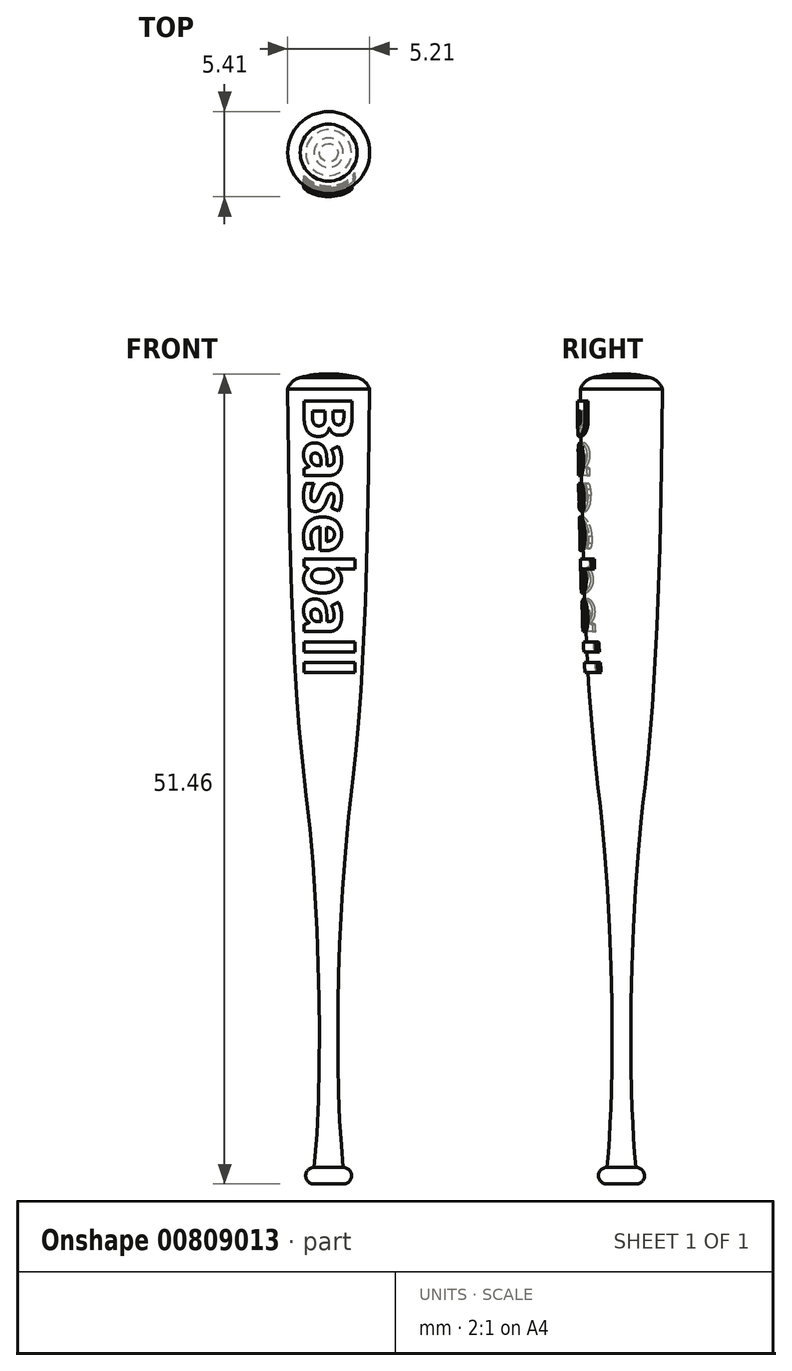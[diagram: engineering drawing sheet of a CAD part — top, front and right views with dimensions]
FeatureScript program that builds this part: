
annotation { "Feature Type Name" : "Feature", "Feature Type Description" : "" }
export const myFeature = defineFeature(function(context is Context, id is Id, definition is map)
    precondition{}
    {
        {
            var Q0;
            Q0=qCreatedBy(makeId("Front.planeOp"),FACE);
            var sketch = newSketch(context, id + "F0", { "sketchPlane" : qUnion([Q0])});
            skFitSpline(sketch, "E0", {"points": [v(-3.44, 24.76) * mm, v(-4.8, -2.6) * mm, v(-5.43, -13.25) * mm, v(-5.12, -24.67) * mm], "startDerivative": vector(-1.3, -133.52) * mm, "endDerivative": vector(3.27, -30.05) * mm});
            skArc(sketch, "E1", {"start": v(-3.44, 24.76) * mm, "mid": v(-3.74, 25.24) * mm, "end": v(-4.24, 25.5) * mm});
            skArc(sketch, "E2", {"start": v(-5.12, -25.72) * mm, "mid": v(-4.59, -25.2) * mm, "end": v(-5.12, -24.67) * mm});
            skArc(sketch, "E3", {"start": v(-4.24, 25.5) * mm, "mid": v(-5.14, 25.68) * mm, "end": v(-6.05, 25.74) * mm});
            skLineSegment(sketch, "E4", {"start": v(-6.05, -25.72) * mm, "end": v(-5.12, -25.72) * mm});
            skFitSpline(sketch, "E5", {"points": [v(6.48, 24.76) * mm, v(5.45, -2.22) * mm, v(4.49, -13.25) * mm, v(4.8, -24.67) * mm], "startDerivative": vector(-1.07, -189.4) * mm, "endDerivative": vector(3.27, -30.05) * mm});
            skArc(sketch, "E6", {"start": v(6.48, 24.76) * mm, "mid": v(6.18, 25.24) * mm, "end": v(5.68, 25.5) * mm});
            skArc(sketch, "E7", {"start": v(4.8, -25.72) * mm, "mid": v(5.33, -25.2) * mm, "end": v(4.8, -24.67) * mm});
            skArc(sketch, "E8", {"start": v(5.68, 25.5) * mm, "mid": v(4.79, 25.68) * mm, "end": v(3.87, 25.74) * mm});
            skLineSegment(sketch, "E9", {"start": v(3.87, -25.72) * mm, "end": v(4.8, -25.72) * mm});
            skLineSegment(sketch, "E10", {"start": v(3.87, 25.74) * mm, "end": v(3.87, 24.94) * mm});
            skLineSegment(sketch, "E11", {"start": v(-6.05, 25.74) * mm, "end": v(-6.05, -25.72) * mm});
            skLineSegment(sketch, "E12", {"start": v(3.87, 24.94) * mm, "end": v(3.87, -25.72) * mm});
            skSolve(sketch);
        }
        {
            var Q0;
            Q0=qCreatedBy(makeId("Front.planeOp"),FACE);
            var sketch = newSketch(context, id + "F1", { "sketchPlane" : qUnion([Q0])});
            skText(sketch, "E13", { "text": "Softball", "fontName": "OpenSans-Bold.ttf"});
            skText(sketch, "E14", { "text": "Baseball", "fontName": "OpenSans-Bold.ttf"});
            const initialGuessF1  = {"E13": [0.00236, 0.02362, 0, -1, 0.00307], "E14": [-0.0076, 0.0244, 0, -1, 0.00307]};
            skSetInitialGuess(sketch, initialGuessF1);
            skSolve(sketch);
        }
        {
            var Q0;
            Q0=makeQuery(id+"F0.imprint","IMPRINT",FACE,{"disambiguationData":[TD([[makeQuery(id+"F0.imprint","IMPRINT",EDGE,{"derivedFrom":sQuery(id+"F0.wireOp",EDGE,"E5")}),-1.0]])]});
            var Q1;
            Q1=sQuery(id+"F0.wireOp",EDGE,"E12");
            revolve(context, id + "F2", {"surfaceOperationType" : NewSurfaceOperationType.NEW, "entities" : qUnion([Q0]), "axis" : qUnion([Q1]), "revolveType" : RevolveType.FULL});
        }
        {
            var Q0;
            Q0 = qSketchRegion(id + "F1", true);
            var Q1;
            Q1=makeQuery(id+"F2.opRevolve","SWEPT_BODY",BODY,{"disambiguationData":[OSD([sQuery(id+"F0.wireOp",EDGE,"E5"),sQuery(id+"F0.wireOp",EDGE,"E6"),sQuery(id+"F0.wireOp",EDGE,"E7"),sQuery(id+"F0.wireOp",EDGE,"E8"),sQuery(id+"F0.wireOp",EDGE,"E9"),sQuery(id+"F0.wireOp",EDGE,"E10"),sQuery(id+"F0.wireOp",EDGE,"E12")])]});
            extrude(context, id + "F3", {"entities" : qUnion([Q0]), "operationType" : NewBodyOperationType.INTERSECT, "depth" : 2.8 * mm, "endBoundEntityBody" : qUnion([Q1]), "offsetDistance" : 25 * mm});
        }
        {
            var Q0;
            Q0=makeQuery(id+"F3.boolean.opBoolean","SPLIT",BODY,{"disambiguationData":[OD(0.0)],"derivedFrom":makeQuery(id+"F2.opRevolve","SWEPT_BODY",BODY,{"disambiguationData":[OSD([sQuery(id+"F0.wireOp",EDGE,"E5"),sQuery(id+"F0.wireOp",EDGE,"E6"),sQuery(id+"F0.wireOp",EDGE,"E7"),sQuery(id+"F0.wireOp",EDGE,"E8"),sQuery(id+"F0.wireOp",EDGE,"E9"),sQuery(id+"F0.wireOp",EDGE,"E10"),sQuery(id+"F0.wireOp",EDGE,"E12")])]})});
            var Q1;
            Q1=makeQuery(id+"F3.boolean.opBoolean","SPLIT",BODY,{"disambiguationData":[OD(1.0)],"derivedFrom":makeQuery(id+"F2.opRevolve","SWEPT_BODY",BODY,{"disambiguationData":[OSD([sQuery(id+"F0.wireOp",EDGE,"E5"),sQuery(id+"F0.wireOp",EDGE,"E6"),sQuery(id+"F0.wireOp",EDGE,"E7"),sQuery(id+"F0.wireOp",EDGE,"E8"),sQuery(id+"F0.wireOp",EDGE,"E9"),sQuery(id+"F0.wireOp",EDGE,"E10"),sQuery(id+"F0.wireOp",EDGE,"E12")])]})});
            var Q2;
            Q2=makeQuery(id+"F3.boolean.opBoolean","SPLIT",BODY,{"disambiguationData":[OD(2.0)],"derivedFrom":makeQuery(id+"F2.opRevolve","SWEPT_BODY",BODY,{"disambiguationData":[OSD([sQuery(id+"F0.wireOp",EDGE,"E5"),sQuery(id+"F0.wireOp",EDGE,"E6"),sQuery(id+"F0.wireOp",EDGE,"E7"),sQuery(id+"F0.wireOp",EDGE,"E8"),sQuery(id+"F0.wireOp",EDGE,"E9"),sQuery(id+"F0.wireOp",EDGE,"E10"),sQuery(id+"F0.wireOp",EDGE,"E12")])]})});
            var Q3;
            Q3=makeQuery(id+"F3.boolean.opBoolean","SPLIT",BODY,{"disambiguationData":[OD(3.0)],"derivedFrom":makeQuery(id+"F2.opRevolve","SWEPT_BODY",BODY,{"disambiguationData":[OSD([sQuery(id+"F0.wireOp",EDGE,"E5"),sQuery(id+"F0.wireOp",EDGE,"E6"),sQuery(id+"F0.wireOp",EDGE,"E7"),sQuery(id+"F0.wireOp",EDGE,"E8"),sQuery(id+"F0.wireOp",EDGE,"E9"),sQuery(id+"F0.wireOp",EDGE,"E10"),sQuery(id+"F0.wireOp",EDGE,"E12")])]})});
            var Q4;
            Q4=makeQuery(id+"F3.boolean.opBoolean","SPLIT",BODY,{"disambiguationData":[OD(4.0)],"derivedFrom":makeQuery(id+"F2.opRevolve","SWEPT_BODY",BODY,{"disambiguationData":[OSD([sQuery(id+"F0.wireOp",EDGE,"E5"),sQuery(id+"F0.wireOp",EDGE,"E6"),sQuery(id+"F0.wireOp",EDGE,"E7"),sQuery(id+"F0.wireOp",EDGE,"E8"),sQuery(id+"F0.wireOp",EDGE,"E9"),sQuery(id+"F0.wireOp",EDGE,"E10"),sQuery(id+"F0.wireOp",EDGE,"E12")])]})});
            var Q5;
            Q5=makeQuery(id+"F3.boolean.opBoolean","SPLIT",BODY,{"disambiguationData":[OD(5.0)],"derivedFrom":makeQuery(id+"F2.opRevolve","SWEPT_BODY",BODY,{"disambiguationData":[OSD([sQuery(id+"F0.wireOp",EDGE,"E5"),sQuery(id+"F0.wireOp",EDGE,"E6"),sQuery(id+"F0.wireOp",EDGE,"E7"),sQuery(id+"F0.wireOp",EDGE,"E8"),sQuery(id+"F0.wireOp",EDGE,"E9"),sQuery(id+"F0.wireOp",EDGE,"E10"),sQuery(id+"F0.wireOp",EDGE,"E12")])]})});
            var Q6;
            Q6=makeQuery(id+"F3.boolean.opBoolean","SPLIT",BODY,{"disambiguationData":[OD(6.0)],"derivedFrom":makeQuery(id+"F2.opRevolve","SWEPT_BODY",BODY,{"disambiguationData":[OSD([sQuery(id+"F0.wireOp",EDGE,"E5"),sQuery(id+"F0.wireOp",EDGE,"E6"),sQuery(id+"F0.wireOp",EDGE,"E7"),sQuery(id+"F0.wireOp",EDGE,"E8"),sQuery(id+"F0.wireOp",EDGE,"E9"),sQuery(id+"F0.wireOp",EDGE,"E10"),sQuery(id+"F0.wireOp",EDGE,"E12")])]})});
            var Q7;
            Q7=makeQuery(id+"F3.boolean.opBoolean","SPLIT",BODY,{"disambiguationData":[OD(7.0)],"derivedFrom":makeQuery(id+"F2.opRevolve","SWEPT_BODY",BODY,{"disambiguationData":[OSD([sQuery(id+"F0.wireOp",EDGE,"E5"),sQuery(id+"F0.wireOp",EDGE,"E6"),sQuery(id+"F0.wireOp",EDGE,"E7"),sQuery(id+"F0.wireOp",EDGE,"E8"),sQuery(id+"F0.wireOp",EDGE,"E9"),sQuery(id+"F0.wireOp",EDGE,"E10"),sQuery(id+"F0.wireOp",EDGE,"E12")])]})});
            transform(context, id + "F4", {"entities" : qUnion([Q0, Q1, Q2, Q3, Q4, Q5, Q6, Q7]), "transformType" : TransformType.TRANSLATION_3D, "dx" : 0 * mm, "dy" : -0.2 * mm, "dz" : 0 * mm, "makeCopy" : false});
        }
        {
            var Q0;
            Q0=makeQuery(id+"F0.imprint","IMPRINT",FACE,{"disambiguationData":[TD([[makeQuery(id+"F0.imprint","IMPRINT",EDGE,{"derivedFrom":sQuery(id+"F0.wireOp",EDGE,"E5")}),-1.0]])]});
            var Q1;
            Q1=sQuery(id+"F0.wireOp",EDGE,"E12");
            revolve(context, id + "F5", {"operationType" : NewBodyOperationType.ADD, "surfaceOperationType" : NewSurfaceOperationType.NEW, "entities" : qUnion([Q0]), "axis" : qUnion([Q1]), "revolveType" : RevolveType.FULL});
        }
        {
            var Q0;
            Q0=makeQuery(id+"F0.imprint","IMPRINT",FACE,{"disambiguationData":[TD([[makeQuery(id+"F0.imprint","IMPRINT",EDGE,{"derivedFrom":sQuery(id+"F0.wireOp",EDGE,"E0")}),-1.0]])]});
            var Q1;
            Q1=sQuery(id+"F0.wireOp",EDGE,"E11");
            revolve(context, id + "F6", {"surfaceOperationType" : NewSurfaceOperationType.NEW, "entities" : qUnion([Q0]), "axis" : qUnion([Q1]), "revolveType" : RevolveType.FULL});
        }
        {
            var Q0;
            Q0=makeQuery(id+"F1.imprint","IMPRINT",FACE,{"disambiguationData":[TD([[makeQuery(id+"F1.imprint","IMPRINT",EDGE,{"derivedFrom":sQuery(id+"F1.wireOp",EDGE,"E14.sketch_text.stroke-0")}),-1.0]])]});
            var Q1;
            Q1=makeQuery(id+"F1.imprint","IMPRINT",FACE,{"disambiguationData":[TD([[makeQuery(id+"F1.imprint","IMPRINT",EDGE,{"derivedFrom":sQuery(id+"F1.wireOp",EDGE,"E14.sketch_text.stroke-25")}),-1.0]])]});
            var Q2;
            Q2=makeQuery(id+"F1.imprint","IMPRINT",FACE,{"disambiguationData":[TD([[makeQuery(id+"F1.imprint","IMPRINT",EDGE,{"derivedFrom":sQuery(id+"F1.wireOp",EDGE,"E14.sketch_text.stroke-52")}),-1.0]])]});
            var Q3;
            Q3=makeQuery(id+"F1.imprint","IMPRINT",FACE,{"disambiguationData":[TD([[makeQuery(id+"F1.imprint","IMPRINT",EDGE,{"derivedFrom":sQuery(id+"F1.wireOp",EDGE,"E14.sketch_text.stroke-77")}),-1.0]])]});
            var Q4;
            Q4=makeQuery(id+"F1.imprint","IMPRINT",FACE,{"disambiguationData":[TD([[makeQuery(id+"F1.imprint","IMPRINT",EDGE,{"derivedFrom":sQuery(id+"F1.wireOp",EDGE,"E14.sketch_text.stroke-96")}),-1.0]])]});
            var Q5;
            Q5=makeQuery(id+"F1.imprint","IMPRINT",FACE,{"disambiguationData":[TD([[makeQuery(id+"F1.imprint","IMPRINT",EDGE,{"derivedFrom":sQuery(id+"F1.wireOp",EDGE,"E14.sketch_text.stroke-119")}),-1.0]])]});
            var Q6;
            Q6=makeQuery(id+"F1.imprint","IMPRINT",FACE,{"disambiguationData":[TD([[makeQuery(id+"F1.imprint","IMPRINT",EDGE,{"derivedFrom":sQuery(id+"F1.wireOp",EDGE,"E14.sketch_text.stroke-146")}),-1.0]])]});
            var Q7;
            Q7=makeQuery(id+"F1.imprint","IMPRINT",FACE,{"disambiguationData":[TD([[makeQuery(id+"F1.imprint","IMPRINT",EDGE,{"derivedFrom":sQuery(id+"F1.wireOp",EDGE,"E14.sketch_text.stroke-150")}),-1.0]])]});
            extrude(context, id + "F7", {"entities" : qUnion([Q0, Q1, Q2, Q3, Q4, Q5, Q6, Q7]), "operationType" : NewBodyOperationType.INTERSECT, "depth" : 25 * mm, "offsetDistance" : 25 * mm});
        }
        {
            var Q0;
            Q0=makeQuery(id+"F7.boolean.opBoolean","SPLIT",BODY,{"disambiguationData":[OD(0.0)],"derivedFrom":makeQuery(id+"F6.opRevolve","SWEPT_BODY",BODY,{"disambiguationData":[OSD([sQuery(id+"F0.wireOp",EDGE,"E0"),sQuery(id+"F0.wireOp",EDGE,"E1"),sQuery(id+"F0.wireOp",EDGE,"E2"),sQuery(id+"F0.wireOp",EDGE,"E3"),sQuery(id+"F0.wireOp",EDGE,"E4"),sQuery(id+"F0.wireOp",EDGE,"E11")])]})});
            var Q1;
            Q1=makeQuery(id+"F7.boolean.opBoolean","SPLIT",BODY,{"disambiguationData":[OD(1.0)],"derivedFrom":makeQuery(id+"F6.opRevolve","SWEPT_BODY",BODY,{"disambiguationData":[OSD([sQuery(id+"F0.wireOp",EDGE,"E0"),sQuery(id+"F0.wireOp",EDGE,"E1"),sQuery(id+"F0.wireOp",EDGE,"E2"),sQuery(id+"F0.wireOp",EDGE,"E3"),sQuery(id+"F0.wireOp",EDGE,"E4"),sQuery(id+"F0.wireOp",EDGE,"E11")])]})});
            var Q2;
            Q2=makeQuery(id+"F7.boolean.opBoolean","SPLIT",BODY,{"disambiguationData":[OD(2.0)],"derivedFrom":makeQuery(id+"F6.opRevolve","SWEPT_BODY",BODY,{"disambiguationData":[OSD([sQuery(id+"F0.wireOp",EDGE,"E0"),sQuery(id+"F0.wireOp",EDGE,"E1"),sQuery(id+"F0.wireOp",EDGE,"E2"),sQuery(id+"F0.wireOp",EDGE,"E3"),sQuery(id+"F0.wireOp",EDGE,"E4"),sQuery(id+"F0.wireOp",EDGE,"E11")])]})});
            var Q3;
            Q3=makeQuery(id+"F7.boolean.opBoolean","SPLIT",BODY,{"disambiguationData":[OD(3.0)],"derivedFrom":makeQuery(id+"F6.opRevolve","SWEPT_BODY",BODY,{"disambiguationData":[OSD([sQuery(id+"F0.wireOp",EDGE,"E0"),sQuery(id+"F0.wireOp",EDGE,"E1"),sQuery(id+"F0.wireOp",EDGE,"E2"),sQuery(id+"F0.wireOp",EDGE,"E3"),sQuery(id+"F0.wireOp",EDGE,"E4"),sQuery(id+"F0.wireOp",EDGE,"E11")])]})});
            var Q4;
            Q4=makeQuery(id+"F7.boolean.opBoolean","SPLIT",BODY,{"disambiguationData":[OD(4.0)],"derivedFrom":makeQuery(id+"F6.opRevolve","SWEPT_BODY",BODY,{"disambiguationData":[OSD([sQuery(id+"F0.wireOp",EDGE,"E0"),sQuery(id+"F0.wireOp",EDGE,"E1"),sQuery(id+"F0.wireOp",EDGE,"E2"),sQuery(id+"F0.wireOp",EDGE,"E3"),sQuery(id+"F0.wireOp",EDGE,"E4"),sQuery(id+"F0.wireOp",EDGE,"E11")])]})});
            var Q5;
            Q5=makeQuery(id+"F7.boolean.opBoolean","SPLIT",BODY,{"disambiguationData":[OD(5.0)],"derivedFrom":makeQuery(id+"F6.opRevolve","SWEPT_BODY",BODY,{"disambiguationData":[OSD([sQuery(id+"F0.wireOp",EDGE,"E0"),sQuery(id+"F0.wireOp",EDGE,"E1"),sQuery(id+"F0.wireOp",EDGE,"E2"),sQuery(id+"F0.wireOp",EDGE,"E3"),sQuery(id+"F0.wireOp",EDGE,"E4"),sQuery(id+"F0.wireOp",EDGE,"E11")])]})});
            var Q6;
            Q6=makeQuery(id+"F7.boolean.opBoolean","SPLIT",BODY,{"disambiguationData":[OD(6.0)],"derivedFrom":makeQuery(id+"F6.opRevolve","SWEPT_BODY",BODY,{"disambiguationData":[OSD([sQuery(id+"F0.wireOp",EDGE,"E0"),sQuery(id+"F0.wireOp",EDGE,"E1"),sQuery(id+"F0.wireOp",EDGE,"E2"),sQuery(id+"F0.wireOp",EDGE,"E3"),sQuery(id+"F0.wireOp",EDGE,"E4"),sQuery(id+"F0.wireOp",EDGE,"E11")])]})});
            var Q7;
            Q7=makeQuery(id+"F7.boolean.opBoolean","SPLIT",BODY,{"disambiguationData":[OD(7.0)],"derivedFrom":makeQuery(id+"F6.opRevolve","SWEPT_BODY",BODY,{"disambiguationData":[OSD([sQuery(id+"F0.wireOp",EDGE,"E0"),sQuery(id+"F0.wireOp",EDGE,"E1"),sQuery(id+"F0.wireOp",EDGE,"E2"),sQuery(id+"F0.wireOp",EDGE,"E3"),sQuery(id+"F0.wireOp",EDGE,"E4"),sQuery(id+"F0.wireOp",EDGE,"E11")])]})});
            transform(context, id + "F8", {"entities" : qUnion([Q0, Q1, Q2, Q3, Q4, Q5, Q6, Q7]), "transformType" : TransformType.TRANSLATION_3D, "dx" : 0 * mm, "dy" : -0.2 * mm, "dz" : 0 * mm, "makeCopy" : false});
        }
        {
            var Q0;
            Q0=makeQuery(id+"F0.imprint","IMPRINT",FACE,{"disambiguationData":[TD([[makeQuery(id+"F0.imprint","IMPRINT",EDGE,{"derivedFrom":sQuery(id+"F0.wireOp",EDGE,"E0")}),-1.0]])]});
            var Q1;
            Q1=sQuery(id+"F0.wireOp",EDGE,"E11");
            revolve(context, id + "F9", {"operationType" : NewBodyOperationType.ADD, "surfaceOperationType" : NewSurfaceOperationType.NEW, "entities" : qUnion([Q0]), "axis" : qUnion([Q1]), "revolveType" : RevolveType.FULL});
        }
    });
